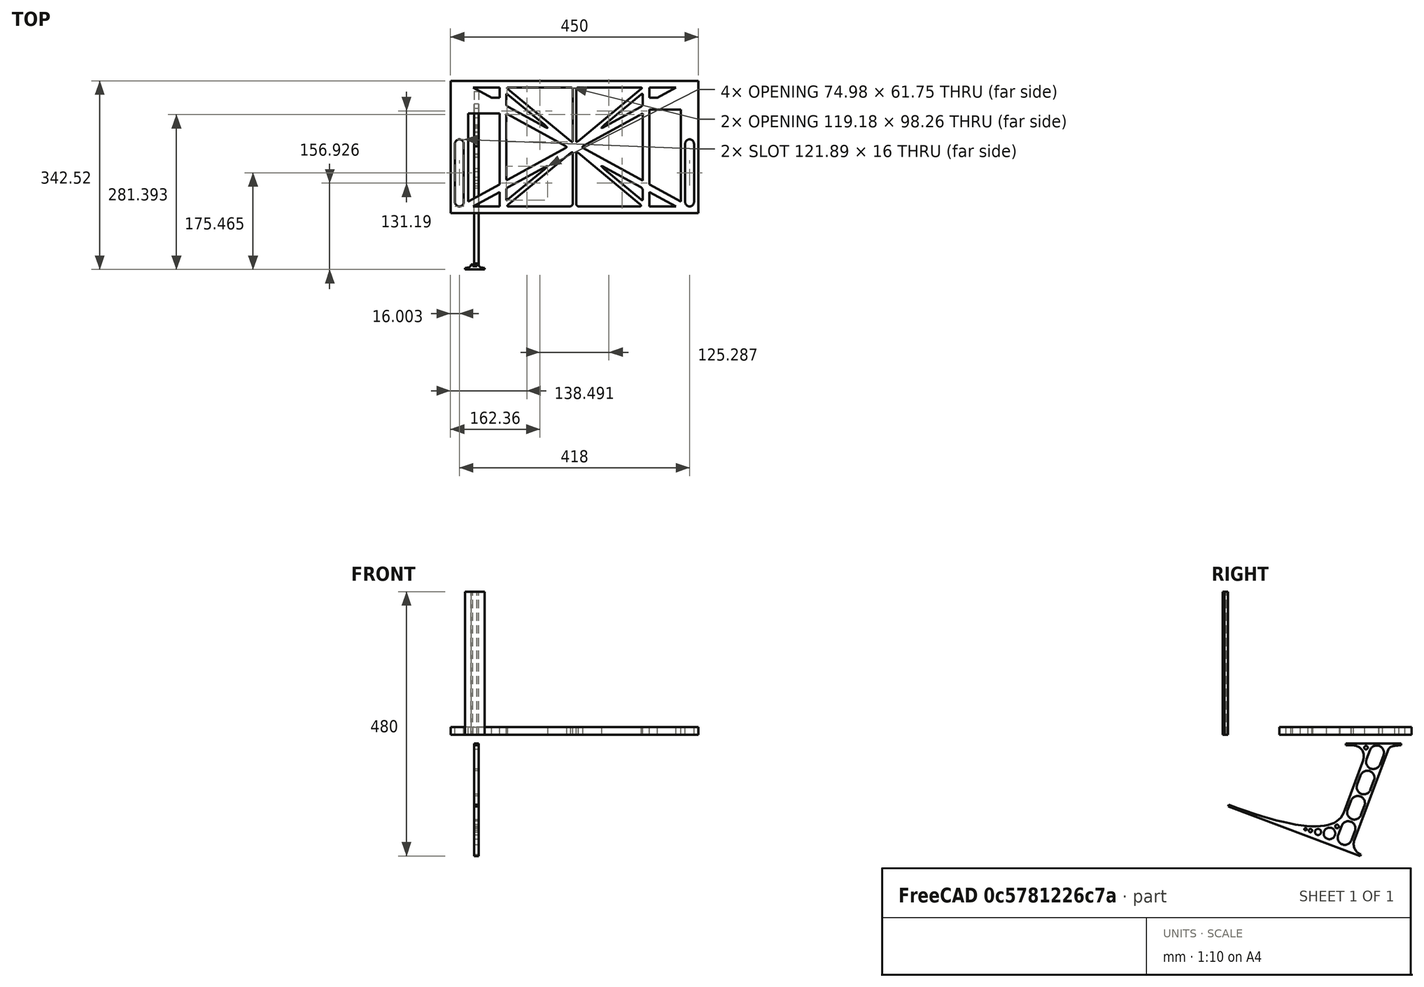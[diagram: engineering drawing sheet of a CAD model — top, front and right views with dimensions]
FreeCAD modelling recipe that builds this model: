
FCSTD DOCUMENT  (FreeCAD 0.19R0.19.2)
Label: laptopStand089
License: All rights reserved
LicenseURL: http://en.wikipedia.org/wiki/All_rights_reserved
objects: Sketcher::SketchObject×3, Part::Extrusion×3
note: 6 computed .brp shape members not serialized (recipe doc carries the construction recipe); baked Part::Feature solids carry a one-line shape summary decoded from their .brp

FEATURE [Sketcher::SketchObject] Sketch
  FullyConstrained = false
  sketch-geometry (236):
    g0: LineSegment StartX=-10.9272 StartY=-82.7794 StartZ=0 EndX=46.0728 EndY=-51.4823 EndZ=0
    g1: LineSegment StartX=366.073 StartY=-91.7794 StartZ=0 EndX=318.073 EndY=-65.424 EndZ=0
    g2: LineSegment StartX=-10.9272 StartY=77.3346 StartZ=0 EndX=-10.9272 EndY=-82.7794 EndZ=0
    g3: LineSegment StartX=375.073 StartY=-82.7794 StartZ=0 EndX=375.073 EndY=83.9235 EndZ=0
    g4: LineSegment StartX=-1.92719 StartY=-91.7794 StartZ=0 EndX=46.0728 EndY=-91.7794 EndZ=0
    g5: LineSegment StartX=318.073 StartY=124.221 StartZ=0 EndX=366.073 EndY=124.221 EndZ=0
    g6: LineSegment StartX=306.073 StartY=77.3346 StartZ=0 EndX=306.073 EndY=-44.8935 EndZ=0
    g7: LineSegment StartX=318.073 StartY=83.9235 StartZ=0 EndX=318.073 EndY=-51.4823 EndZ=0
    g8: LineSegment StartX=318.073 StartY=-51.4823 StartZ=0 EndX=375.073 EndY=-82.7794 EndZ=0
    g9: LineSegment StartX=318.073 StartY=-65.424 StartZ=0 EndX=318.073 EndY=-91.7794 EndZ=0
    g10: LineSegment StartX=318.073 StartY=-91.7794 StartZ=0 EndX=366.073 EndY=-91.7794 EndZ=0
    g11: LineSegment StartX=46.0728 StartY=-65.424 StartZ=0 EndX=-1.92719 EndY=-91.7794 EndZ=0
    g12: LineSegment StartX=46.0728 StartY=-65.424 StartZ=0 EndX=46.0728 EndY=-91.7794 EndZ=0
    g13: LineSegment StartX=46.0728 StartY=77.3346 StartZ=0 EndX=46.0728 EndY=-51.4823 EndZ=0
    g14: LineSegment StartX=-42.9272 StartY=136.221 StartZ=0 EndX=-42.9272 EndY=-103.779 EndZ=0
    g15: LineSegment StartX=407.073 StartY=136.221 StartZ=0 EndX=407.073 EndY=-103.779 EndZ=0
    g16: ArcOfCircle CenterX=-26.9272 CenterY=22.1087 CenterZ=0 NormalX=0 NormalY=0 NormalZ=1 AngleXU=0 Radius=8 StartAngle=1e-16 EndAngle=3.14159
    g17: ArcOfCircle CenterX=-26.9272 CenterY=-83.7794 CenterZ=0 NormalX=0 NormalY=0 NormalZ=1 AngleXU=0 Radius=8 StartAngle=3.14159 EndAngle=6.28319
    g18: LineSegment StartX=-34.9272 StartY=22.1087 StartZ=0 EndX=-34.9272 EndY=-83.7794 EndZ=0
    g19: LineSegment StartX=-18.9272 StartY=22.1087 StartZ=0 EndX=-18.9272 EndY=-83.7794 EndZ=0
    g20: ArcOfCircle CenterX=391.073 CenterY=22.1087 CenterZ=0 NormalX=0 NormalY=0 NormalZ=1 AngleXU=0 Radius=8 StartAngle=-4.4e-15 EndAngle=3.14159
    g21: LineSegment StartX=399.073 StartY=22.1087 StartZ=0 EndX=399.073 EndY=-83.7794 EndZ=0
    g22: LineSegment StartX=383.073 StartY=22.1087 StartZ=0 EndX=383.073 EndY=-83.7794 EndZ=0
    g23: ArcOfCircle CenterX=391.073 CenterY=-83.7794 CenterZ=0 NormalX=0 NormalY=0 NormalZ=1 AngleXU=0 Radius=8 StartAngle=3.14159 EndAngle=6.28319
    g24: Circle CenterX=175.022 CenterY=27.0628 CenterZ=0 NormalX=0 NormalY=0 NormalZ=1 AngleXU=0 Radius=1
    g25: Circle CenterX=179.022 CenterY=24.8665 CenterZ=0 NormalX=0 NormalY=0 NormalZ=1 AngleXU=0 Radius=1
    g26: Circle CenterX=179.022 CenterY=27.0628 CenterZ=0 NormalX=0 NormalY=0 NormalZ=1 AngleXU=0 Radius=1
    g27: BSplineCurve PolesCount=3 KnotsCount=2 Degree=2 IsPeriodic=0
    g28: GeomPoint X=175.022 Y=27.0628 Z=0
    g29: GeomPoint X=179.022 Y=27.0628 Z=0
    g30: Circle CenterX=189.124 CenterY=27.0628 CenterZ=0 NormalX=0 NormalY=0 NormalZ=1 AngleXU=0 Radius=1
    g31: Circle CenterX=185.124 CenterY=24.8665 CenterZ=0 NormalX=0 NormalY=0 NormalZ=1 AngleXU=0 Radius=1
    g32: Circle CenterX=185.124 CenterY=27.0628 CenterZ=0 NormalX=0 NormalY=0 NormalZ=1 AngleXU=0 Radius=1
    g33: BSplineCurve PolesCount=3 KnotsCount=2 Degree=2 IsPeriodic=0
    g34: GeomPoint X=189.124 Y=27.0628 Z=0
    g35: GeomPoint X=185.124 Y=27.0628 Z=0
    g36: Circle CenterX=175.022 CenterY=5.37834 CenterZ=0 NormalX=0 NormalY=0 NormalZ=1 AngleXU=0 Radius=1
    g37: Circle CenterX=179.022 CenterY=7.57463 CenterZ=0 NormalX=0 NormalY=0 NormalZ=1 AngleXU=0 Radius=1
    g38: Circle CenterX=179.022 CenterY=5.34704 CenterZ=0 NormalX=0 NormalY=0 NormalZ=1 AngleXU=0 Radius=1
    g39: BSplineCurve PolesCount=3 KnotsCount=2 Degree=2 IsPeriodic=0
    g40: GeomPoint X=175.022 Y=5.37834 Z=0
    g41: GeomPoint X=179.022 Y=5.34704 Z=0
    g42: Circle CenterX=189.124 CenterY=5.37834 CenterZ=0 NormalX=0 NormalY=0 NormalZ=1 AngleXU=0 Radius=1
    g43: Circle CenterX=185.124 CenterY=7.57463 CenterZ=0 NormalX=0 NormalY=0 NormalZ=1 AngleXU=0 Radius=1
    g44: Circle CenterX=185.124 CenterY=5.34704 CenterZ=0 NormalX=0 NormalY=0 NormalZ=1 AngleXU=0 Radius=1
    g45: BSplineCurve PolesCount=3 KnotsCount=2 Degree=2 IsPeriodic=0
    g46: GeomPoint X=189.124 Y=5.37834 Z=0
    g47: GeomPoint X=185.124 Y=5.34704 Z=0
    g48: Circle CenterX=165.871 CenterY=18.1458 CenterZ=0 NormalX=0 NormalY=0 NormalZ=1 AngleXU=0 Radius=1
    g49: Circle CenterX=169.377 CenterY=16.2206 CenterZ=0 NormalX=0 NormalY=0 NormalZ=1 AngleXU=0 Radius=1
    g50: Circle CenterX=165.871 CenterY=14.2954 CenterZ=0 NormalX=0 NormalY=0 NormalZ=1 AngleXU=0 Radius=1
    g51: BSplineCurve PolesCount=3 KnotsCount=2 Degree=2 IsPeriodic=0
    g52: GeomPoint X=165.871 Y=18.1458 Z=0
    g53: GeomPoint X=165.871 Y=14.2954 Z=0
    g54: Circle CenterX=198.275 CenterY=18.1458 CenterZ=0 NormalX=0 NormalY=0 NormalZ=1 AngleXU=0 Radius=1
    g55: Circle CenterX=194.768 CenterY=16.2206 CenterZ=0 NormalX=0 NormalY=0 NormalZ=1 AngleXU=0 Radius=1
    g56: Circle CenterX=198.275 CenterY=14.2954 CenterZ=0 NormalX=0 NormalY=0 NormalZ=1 AngleXU=0 Radius=1
    g57: BSplineCurve PolesCount=3 KnotsCount=2 Degree=2 IsPeriodic=0
    g58: GeomPoint X=198.275 Y=18.1458 Z=0
    g59: GeomPoint X=198.275 Y=14.2954 Z=0
    g60: LineSegment StartX=198.275 StartY=18.1458 StartZ=0 EndX=306.073 EndY=77.3346 EndZ=0
    g61: LineSegment StartX=198.275 StartY=14.2954 StartZ=0 EndX=306.073 EndY=-44.8935 EndZ=0
    g62: LineSegment StartX=407.073 StartY=-103.779 StartZ=0 EndX=-42.9272 EndY=-103.779 EndZ=0
    g63: LineSegment StartX=407.073 StartY=136.221 StartZ=0 EndX=-42.9272 EndY=136.221 EndZ=0
    g64: LineSegment StartX=46.0728 StartY=77.3346 StartZ=0 EndX=-10.9272 EndY=77.3346 EndZ=0
    g65: LineSegment StartX=46.0728 StartY=105.865 StartZ=0 EndX=31.5028 EndY=105.865 EndZ=0
    g66: LineSegment StartX=46.0728 StartY=124.221 StartZ=0 EndX=46.0728 EndY=105.865 EndZ=0
    g67: LineSegment StartX=-1.92719 StartY=124.221 StartZ=0 EndX=31.5028 EndY=105.865 EndZ=0
    g68: LineSegment StartX=46.0728 StartY=124.221 StartZ=0 EndX=-1.92719 EndY=124.221 EndZ=0
    g69: LineSegment StartX=318.073 StartY=83.9235 StartZ=0 EndX=375.073 EndY=83.9235 EndZ=0
    g70: LineSegment StartX=318.073 StartY=105.865 StartZ=0 EndX=332.643 EndY=105.865 EndZ=0
    g71: LineSegment StartX=332.643 StartY=105.865 StartZ=0 EndX=366.073 EndY=124.221 EndZ=0
    g72: LineSegment StartX=318.073 StartY=124.221 StartZ=0 EndX=318.073 EndY=105.865 EndZ=0
    g73: Circle CenterX=125.607 CenterY=54.1951 CenterZ=0 NormalX=0 NormalY=0 NormalZ=1 AngleXU=0 Radius=1
    g74: Circle CenterX=139.632 CenterY=46.4944 CenterZ=0 NormalX=0 NormalY=0 NormalZ=1 AngleXU=0 Radius=1
    g75: Circle CenterX=127.326 CenterY=56.7187 CenterZ=0 NormalX=0 NormalY=0 NormalZ=1 AngleXU=0 Radius=1
    g76: BSplineCurve PolesCount=3 KnotsCount=2 Degree=2 IsPeriodic=0
    g77: GeomPoint X=125.607 Y=54.1951 Z=0
    g78: GeomPoint X=127.326 Y=56.7187 Z=0
    g79: Circle CenterX=236.821 CenterY=56.7187 CenterZ=0 NormalX=0 NormalY=0 NormalZ=1 AngleXU=0 Radius=1
    g80: Circle CenterX=224.513 CenterY=46.4944 CenterZ=0 NormalX=0 NormalY=0 NormalZ=1 AngleXU=0 Radius=1
    g81: Circle CenterX=238.538 CenterY=54.1951 CenterZ=0 NormalX=0 NormalY=0 NormalZ=1 AngleXU=0 Radius=1
    g82: BSplineCurve PolesCount=3 KnotsCount=2 Degree=2 IsPeriodic=0
    g83: GeomPoint X=236.821 Y=56.7187 Z=0
    g84: GeomPoint X=238.538 Y=54.1951 Z=0
    g85: Circle CenterX=238.538 CenterY=-21.7539 CenterZ=0 NormalX=0 NormalY=0 NormalZ=1 AngleXU=0 Radius=1
    g86: Circle CenterX=224.513 CenterY=-14.0532 CenterZ=0 NormalX=0 NormalY=0 NormalZ=1 AngleXU=0 Radius=1
    g87: Circle CenterX=236.821 CenterY=-24.2775 CenterZ=0 NormalX=0 NormalY=0 NormalZ=1 AngleXU=0 Radius=1
    g88: BSplineCurve PolesCount=3 KnotsCount=2 Degree=2 IsPeriodic=0
    g89: GeomPoint X=238.538 Y=-21.7539 Z=0
    g90: GeomPoint X=236.821 Y=-24.2775 Z=0
    g91: Circle CenterX=125.607 CenterY=-21.7539 CenterZ=0 NormalX=0 NormalY=0 NormalZ=1 AngleXU=0 Radius=1
    g92: Circle CenterX=139.632 CenterY=-14.0532 CenterZ=0 NormalX=0 NormalY=0 NormalZ=1 AngleXU=0 Radius=1
    g93: Circle CenterX=127.325 CenterY=-24.2775 CenterZ=0 NormalX=0 NormalY=0 NormalZ=1 AngleXU=0 Radius=1
    g94: BSplineCurve PolesCount=3 KnotsCount=2 Degree=2 IsPeriodic=0
    g95: GeomPoint X=125.607 Y=-21.7539 Z=0
    g96: GeomPoint X=127.325 Y=-24.2775 Z=0
    g97: Circle CenterX=302.996 CenterY=111.695 CenterZ=0 NormalX=0 NormalY=0 NormalZ=1 AngleXU=0 Radius=1
    g98: Circle CenterX=306.073 CenterY=114.251 CenterZ=0 NormalX=0 NormalY=0 NormalZ=1 AngleXU=0 Radius=1
    g99: Circle CenterX=306.073 CenterY=110.251 CenterZ=0 NormalX=0 NormalY=0 NormalZ=1 AngleXU=0 Radius=1
    g100: BSplineCurve PolesCount=3 KnotsCount=2 Degree=2 IsPeriodic=0
    g101: GeomPoint X=302.996 Y=111.695 Z=0
    g102: GeomPoint X=306.073 Y=110.251 Z=0
    g103: Circle CenterX=306.073 CenterY=95.2763 CenterZ=0 NormalX=0 NormalY=0 NormalZ=1 AngleXU=0 Radius=1
    g104: Circle CenterX=306.073 CenterY=91.2763 CenterZ=0 NormalX=0 NormalY=0 NormalZ=1 AngleXU=0 Radius=1
    g105: Circle CenterX=302.567 CenterY=89.3511 CenterZ=0 NormalX=0 NormalY=0 NormalZ=1 AngleXU=0 Radius=1
    g106: BSplineCurve PolesCount=3 KnotsCount=2 Degree=2 IsPeriodic=0
    g107: GeomPoint X=306.073 Y=95.2763 Z=0
    g108: GeomPoint X=302.567 Y=89.3511 Z=0
    g109: LineSegment StartX=306.073 StartY=110.251 StartZ=0 EndX=306.073 EndY=95.2763 EndZ=0
    g110: LineSegment StartX=302.996 StartY=111.695 StartZ=0 EndX=236.821 EndY=56.7187 EndZ=0
    g111: LineSegment StartX=238.538 StartY=54.1951 StartZ=0 EndX=302.567 EndY=89.3511 EndZ=0
    g112: Circle CenterX=61.1496 CenterY=111.695 CenterZ=0 NormalX=0 NormalY=0 NormalZ=1 AngleXU=0 Radius=1
    g113: Circle CenterX=58.0728 CenterY=114.251 CenterZ=0 NormalX=0 NormalY=0 NormalZ=1 AngleXU=0 Radius=1
    g114: Circle CenterX=58.0728 CenterY=110.251 CenterZ=0 NormalX=0 NormalY=0 NormalZ=1 AngleXU=0 Radius=1
    g115: BSplineCurve PolesCount=3 KnotsCount=2 Degree=2 IsPeriodic=0
    g116: GeomPoint X=61.1496 Y=111.695 Z=0
    g117: GeomPoint X=58.0728 Y=110.251 Z=0
    g118: Circle CenterX=61.5791 CenterY=89.3511 CenterZ=0 NormalX=0 NormalY=0 NormalZ=1 AngleXU=0 Radius=1
    g119: Circle CenterX=58.0728 CenterY=91.2763 CenterZ=0 NormalX=0 NormalY=0 NormalZ=1 AngleXU=0 Radius=1
    g120: Circle CenterX=58.0728 CenterY=95.2763 CenterZ=0 NormalX=0 NormalY=0 NormalZ=1 AngleXU=0 Radius=1
    g121: BSplineCurve PolesCount=3 KnotsCount=2 Degree=2 IsPeriodic=0
    g122: GeomPoint X=61.5791 Y=89.3511 Z=0
    g123: GeomPoint X=58.0728 Y=95.2763 Z=0
    g124: LineSegment StartX=58.0728 StartY=110.251 StartZ=0 EndX=58.0728 EndY=95.2763 EndZ=0
    g125: LineSegment StartX=61.1496 StartY=111.695 StartZ=0 EndX=127.326 EndY=56.7187 EndZ=0
    g126: LineSegment StartX=125.607 StartY=54.1951 StartZ=0 EndX=61.5791 EndY=89.3511 EndZ=0
    g127: Circle CenterX=61.5791 CenterY=-56.9099 CenterZ=0 NormalX=0 NormalY=0 NormalZ=1 AngleXU=0 Radius=1
    g128: Circle CenterX=58.0728 CenterY=-58.8351 CenterZ=0 NormalX=0 NormalY=0 NormalZ=1 AngleXU=0 Radius=1
    g129: Circle CenterX=58.0728 CenterY=-62.8351 CenterZ=0 NormalX=0 NormalY=0 NormalZ=1 AngleXU=0 Radius=1
    g130: BSplineCurve PolesCount=3 KnotsCount=2 Degree=2 IsPeriodic=0
    g131: GeomPoint X=61.5791 Y=-56.9099 Z=0
    g132: GeomPoint X=58.0728 Y=-62.8351 Z=0
    g133: Circle CenterX=58.0728 CenterY=-77.8102 CenterZ=0 NormalX=0 NormalY=0 NormalZ=1 AngleXU=0 Radius=1
    g134: Circle CenterX=58.0728 CenterY=-81.8102 CenterZ=0 NormalX=0 NormalY=0 NormalZ=1 AngleXU=0 Radius=1
    g135: Circle CenterX=61.1496 CenterY=-79.2541 CenterZ=0 NormalX=0 NormalY=0 NormalZ=1 AngleXU=0 Radius=1
    g136: BSplineCurve PolesCount=3 KnotsCount=2 Degree=2 IsPeriodic=0
    g137: GeomPoint X=58.0728 Y=-77.8102 Z=0
    g138: GeomPoint X=61.1496 Y=-79.2541 Z=0
    g139: LineSegment StartX=58.0728 StartY=-62.8351 StartZ=0 EndX=58.0728 EndY=-77.8102 EndZ=0
    g140: LineSegment StartX=61.1496 StartY=-79.2541 StartZ=0 EndX=127.325 EndY=-24.2775 EndZ=0
    g141: LineSegment StartX=125.607 StartY=-21.7539 StartZ=0 EndX=61.5791 EndY=-56.9099 EndZ=0
    g142: Circle CenterX=302.567 CenterY=-56.9099 CenterZ=0 NormalX=0 NormalY=0 NormalZ=1 AngleXU=0 Radius=1
    g143: Circle CenterX=306.073 CenterY=-58.8351 CenterZ=0 NormalX=0 NormalY=0 NormalZ=1 AngleXU=0 Radius=1
    g144: Circle CenterX=306.073 CenterY=-62.8351 CenterZ=0 NormalX=0 NormalY=0 NormalZ=1 AngleXU=0 Radius=1
    g145: BSplineCurve PolesCount=3 KnotsCount=2 Degree=2 IsPeriodic=0
    g146: GeomPoint X=302.567 Y=-56.9099 Z=0
    g147: GeomPoint X=306.073 Y=-62.8351 Z=0
    g148: Circle CenterX=302.996 CenterY=-79.2541 CenterZ=0 NormalX=0 NormalY=0 NormalZ=1 AngleXU=0 Radius=1
    g149: Circle CenterX=306.073 CenterY=-81.8102 CenterZ=0 NormalX=0 NormalY=0 NormalZ=1 AngleXU=0 Radius=1
    g150: Circle CenterX=306.073 CenterY=-77.8102 CenterZ=0 NormalX=0 NormalY=0 NormalZ=1 AngleXU=0 Radius=1
    g151: BSplineCurve PolesCount=3 KnotsCount=2 Degree=2 IsPeriodic=0
    g152: GeomPoint X=302.996 Y=-79.2541 Z=0
    g153: GeomPoint X=306.073 Y=-77.8102 Z=0
    g154: LineSegment StartX=306.073 StartY=-62.8351 StartZ=0 EndX=306.073 EndY=-77.8102 EndZ=0
    g155: LineSegment StartX=302.996 StartY=-79.2541 StartZ=0 EndX=236.821 EndY=-24.2775 EndZ=0
    g156: LineSegment StartX=238.538 StartY=-21.7539 StartZ=0 EndX=302.567 EndY=-56.9099 EndZ=0
    g157: Circle CenterX=61.6457 CenterY=-88.8112 CenterZ=0 NormalX=0 NormalY=0 NormalZ=1 AngleXU=0 Radius=1
    g158: Circle CenterX=58.0728 CenterY=-91.7794 CenterZ=0 NormalX=0 NormalY=0 NormalZ=1 AngleXU=0 Radius=1
    g159: Circle CenterX=63.9135 CenterY=-91.7794 CenterZ=0 NormalX=0 NormalY=0 NormalZ=1 AngleXU=0 Radius=1
    g160: BSplineCurve PolesCount=3 KnotsCount=2 Degree=2 IsPeriodic=0
    g161: GeomPoint X=61.6457 Y=-88.8112 Z=0
    g162: GeomPoint X=63.9135 Y=-91.7794 Z=0
    g163: Circle CenterX=179.022 CenterY=-85.8163 CenterZ=0 NormalX=0 NormalY=0 NormalZ=1 AngleXU=0 Radius=1
    g164: Circle CenterX=179.022 CenterY=-91.7794 CenterZ=0 NormalX=0 NormalY=0 NormalZ=1 AngleXU=0 Radius=1
    g165: Circle CenterX=171.895 CenterY=-91.7794 CenterZ=0 NormalX=0 NormalY=0 NormalZ=1 AngleXU=0 Radius=1
    g166: BSplineCurve PolesCount=3 KnotsCount=2 Degree=2 IsPeriodic=0
    g167: GeomPoint X=179.022 Y=-85.8163 Z=0
    g168: GeomPoint X=171.895 Y=-91.7794 Z=0
    g169: Circle CenterX=185.124 CenterY=-86.2028 CenterZ=0 NormalX=0 NormalY=0 NormalZ=1 AngleXU=0 Radius=1
    g170: Circle CenterX=185.124 CenterY=-91.7794 CenterZ=0 NormalX=0 NormalY=0 NormalZ=1 AngleXU=0 Radius=1
    g171: Circle CenterX=191.747 CenterY=-91.7794 CenterZ=0 NormalX=0 NormalY=0 NormalZ=1 AngleXU=0 Radius=1
    g172: BSplineCurve PolesCount=3 KnotsCount=2 Degree=2 IsPeriodic=0
    g173: GeomPoint X=185.124 Y=-86.2028 Z=0
    g174: GeomPoint X=191.747 Y=-91.7794 Z=0
    g175: Circle CenterX=299.888 CenterY=-86.6413 CenterZ=0 NormalX=0 NormalY=0 NormalZ=1 AngleXU=0 Radius=1
    g176: Circle CenterX=306.073 CenterY=-91.7794 CenterZ=0 NormalX=0 NormalY=0 NormalZ=1 AngleXU=0 Radius=1
    g177: Circle CenterX=298.776 CenterY=-91.7794 CenterZ=0 NormalX=0 NormalY=0 NormalZ=1 AngleXU=0 Radius=1
    g178: BSplineCurve PolesCount=3 KnotsCount=2 Degree=2 IsPeriodic=0
    g179: GeomPoint X=299.888 Y=-86.6413 Z=0
    g180: GeomPoint X=298.776 Y=-91.7794 Z=0
    g181: LineSegment StartX=189.124 StartY=5.37834 StartZ=0 EndX=299.888 EndY=-86.6413 EndZ=0
    g182: LineSegment StartX=298.776 StartY=-91.7794 StartZ=0 EndX=191.747 EndY=-91.7794 EndZ=0
    g183: LineSegment StartX=185.124 StartY=-86.2028 StartZ=0 EndX=185.124 EndY=5.34704 EndZ=0
    g184: LineSegment StartX=179.022 StartY=5.34704 StartZ=0 EndX=179.022 EndY=-85.8163 EndZ=0
    g185: LineSegment StartX=171.895 StartY=-91.7794 StartZ=0 EndX=63.9135 EndY=-91.7794 EndZ=0
    g186: LineSegment StartX=61.6457 StartY=-88.8112 StartZ=0 EndX=175.022 EndY=5.37834 EndZ=0
    g187: Circle CenterX=302.073 CenterY=124.221 CenterZ=0 NormalX=0 NormalY=0 NormalZ=1 AngleXU=0 Radius=1
    g188: Circle CenterX=306.073 CenterY=124.221 CenterZ=0 NormalX=0 NormalY=0 NormalZ=1 AngleXU=0 Radius=1
    g189: Circle CenterX=302.996 CenterY=121.665 CenterZ=0 NormalX=0 NormalY=0 NormalZ=1 AngleXU=0 Radius=1
    g190: BSplineCurve PolesCount=3 KnotsCount=2 Degree=2 IsPeriodic=0
    g191: GeomPoint X=302.073 Y=124.221 Z=0
    g192: GeomPoint X=302.996 Y=121.665 Z=0
    g193: Circle CenterX=189.124 CenterY=124.221 CenterZ=0 NormalX=0 NormalY=0 NormalZ=1 AngleXU=0 Radius=1
    g194: Circle CenterX=185.124 CenterY=124.221 CenterZ=0 NormalX=0 NormalY=0 NormalZ=1 AngleXU=0 Radius=1
    g195: Circle CenterX=185.124 CenterY=120.221 CenterZ=0 NormalX=0 NormalY=0 NormalZ=1 AngleXU=0 Radius=1
    g196: BSplineCurve PolesCount=3 KnotsCount=2 Degree=2 IsPeriodic=0
    g197: GeomPoint X=189.124 Y=124.221 Z=0
    g198: GeomPoint X=185.124 Y=120.221 Z=0
    g199: Circle CenterX=175.022 CenterY=124.221 CenterZ=0 NormalX=0 NormalY=0 NormalZ=1 AngleXU=0 Radius=1
    g200: Circle CenterX=179.022 CenterY=124.221 CenterZ=0 NormalX=0 NormalY=0 NormalZ=1 AngleXU=0 Radius=1
    g201: Circle CenterX=179.022 CenterY=120.221 CenterZ=0 NormalX=0 NormalY=0 NormalZ=1 AngleXU=0 Radius=1
    g202: BSplineCurve PolesCount=3 KnotsCount=2 Degree=2 IsPeriodic=0
    g203: GeomPoint X=175.022 Y=124.221 Z=0
    g204: GeomPoint X=179.022 Y=120.221 Z=0
    g205: Circle CenterX=62.0728 CenterY=124.221 CenterZ=0 NormalX=0 NormalY=0 NormalZ=1 AngleXU=0 Radius=1
    g206: Circle CenterX=58.0728 CenterY=124.221 CenterZ=0 NormalX=0 NormalY=0 NormalZ=1 AngleXU=0 Radius=1
    g207: Circle CenterX=61.1496 CenterY=121.665 CenterZ=0 NormalX=0 NormalY=0 NormalZ=1 AngleXU=0 Radius=1
    g208: BSplineCurve PolesCount=3 KnotsCount=2 Degree=2 IsPeriodic=0
    g209: GeomPoint X=62.0728 Y=124.221 Z=0
    g210: GeomPoint X=61.1496 Y=121.665 Z=0
    g211: LineSegment StartX=62.0728 StartY=124.221 StartZ=0 EndX=175.022 EndY=124.221 EndZ=0
    g212: LineSegment StartX=179.022 StartY=120.221 StartZ=0 EndX=179.022 EndY=27.0628 EndZ=0
    g213: LineSegment StartX=185.124 StartY=27.0628 StartZ=0 EndX=185.124 EndY=120.221 EndZ=0
    g214: LineSegment StartX=189.124 StartY=124.221 StartZ=0 EndX=302.073 EndY=124.221 EndZ=0
    g215: LineSegment StartX=302.996 StartY=121.665 StartZ=0 EndX=189.124 EndY=27.0628 EndZ=0
    g216: LineSegment StartX=175.022 StartY=27.0628 StartZ=0 EndX=61.1496 EndY=121.665 EndZ=0
    g217: Circle CenterX=61.5791 CenterY=75.4095 CenterZ=0 NormalX=0 NormalY=0 NormalZ=1 AngleXU=0 Radius=1
    g218: Circle CenterX=58.0728 CenterY=77.3346 CenterZ=0 NormalX=0 NormalY=0 NormalZ=1 AngleXU=0 Radius=1
    g219: Circle CenterX=58.0728 CenterY=73.3346 CenterZ=0 NormalX=0 NormalY=0 NormalZ=1 AngleXU=0 Radius=1
    g220: BSplineCurve PolesCount=3 KnotsCount=2 Degree=2 IsPeriodic=0
    g221: GeomPoint X=61.5791 Y=75.4095 Z=0
    g222: GeomPoint X=58.0728 Y=73.3346 Z=0
    g223: Circle CenterX=58.0728 CenterY=-40.8935 CenterZ=0 NormalX=0 NormalY=0 NormalZ=1 AngleXU=0 Radius=1
    g224: Circle CenterX=58.0728 CenterY=-44.8935 CenterZ=0 NormalX=0 NormalY=0 NormalZ=1 AngleXU=0 Radius=1
    g225: Circle CenterX=61.5791 CenterY=-42.9683 CenterZ=0 NormalX=0 NormalY=0 NormalZ=1 AngleXU=0 Radius=1
    g226: BSplineCurve PolesCount=3 KnotsCount=2 Degree=2 IsPeriodic=0
    g227: GeomPoint X=58.0728 Y=-40.8935 Z=0
    g228: GeomPoint X=61.5791 Y=-42.9683 Z=0
    g229: LineSegment StartX=61.5791 StartY=-42.9683 StartZ=0 EndX=165.871 EndY=14.2954 EndZ=0
    g230: LineSegment StartX=165.871 StartY=18.1458 StartZ=0 EndX=61.5791 EndY=75.4095 EndZ=0
    g231: LineSegment StartX=58.0728 StartY=73.3346 StartZ=0 EndX=58.0728 EndY=-40.8935 EndZ=0
    g232: LineSegment StartX=306.994 StartY=77.7433 StartZ=0 EndX=306.994 EndY=73.7433 EndZ=0
    g233: LineSegment StartX=305.944 StartY=78.0104 StartZ=0 EndX=302.438 EndY=76.0852 EndZ=0
    g234: LineSegment StartX=307.626 StartY=-43.3024 StartZ=0 EndX=307.626 EndY=-39.3024 EndZ=0
    g235: LineSegment StartX=303.392 StartY=-44.772 StartZ=0 EndX=299.886 EndY=-42.8468 EndZ=0
  constraints (403):
    c: Horizontal(g4)
    c: Horizontal(g5)
    c: Coincident(g7,g8)
    c: Coincident(g9,g1)
    c: Tangent(g7,g9)
    c: Coincident(g12,g11)
    c: Coincident(g0,g13)
    c: Block(g8)
    c: Block(g3)
    c: Block(g1)
    c: Block(g9)
    c: Block(g12)
    c: Block(g11)
    c: Block(g0)
    c: Block(g2)
    c: Block(g6)
    c: Block(g5)
    c: Block(g10)
    c: Block(g4)
    c: Vertical(g14)
    c: Vertical(g15)
    c: Block(g15)
    c: Block(g14)
    c: Tangent(g16,g19) = 1.5708
    c: Tangent(g16,g18) = -1.5708
    c: Tangent(g18,g17) = -1.5708
    c: Tangent(g19,g17) = 1.5708
    c: Vertical(g18)
    c: Equal(g16,g17)
    c: Block(g19)
    c: Block(g18)
    c: Tangent(g20,g21) = 1.5708
    c: Tangent(g21,g23) = 1.5708
    c: Equal(g20,g23)
    c: Coincident(g22,g20)
    c: Coincident(g22,g23)
    c: Block(g21)
    c: Block(g22)
    c: Weight(g24) = 1
    c: Equal(g24,g25)
    c: Equal(g24,g26)
    c: InternalAlignment(g24,g27)
    c: InternalAlignment(g25,g27)
    c: InternalAlignment(g26,g27)
    c: InternalAlignment(g28,g27)
    c: InternalAlignment(g29,g27)
    c: Weight(g30) = 1
    c: Equal(g30,g31)
    c: Equal(g30,g32)
    c: InternalAlignment(g30,g33)
    c: InternalAlignment(g31,g33)
    c: InternalAlignment(g32,g33)
    c: InternalAlignment(g34,g33)
    c: InternalAlignment(g35,g33)
    c: Block(g33)
    c: Block(g27)
    c: Weight(g36) = 1
    c: Equal(g36,g37)
    c: Equal(g36,g38)
    c: InternalAlignment(g36,g39)
    c: InternalAlignment(g37,g39)
    c: InternalAlignment(g38,g39)
    c: InternalAlignment(g40,g39)
    c: InternalAlignment(g41,g39)
    c: Weight(g42) = 1
    c: Equal(g42,g43)
    c: Equal(g42,g44)
    c: InternalAlignment(g42,g45)
    c: InternalAlignment(g43,g45)
    c: InternalAlignment(g44,g45)
    c: InternalAlignment(g46,g45)
    c: InternalAlignment(g47,g45)
    c: Block(g45)
    c: Block(g39)
    c: Weight(g48) = 1
    c: Equal(g48,g49)
    c: Equal(g48,g50)
    c: InternalAlignment(g48,g51)
    c: InternalAlignment(g49,g51)
    c: InternalAlignment(g50,g51)
    c: InternalAlignment(g52,g51)
    c: InternalAlignment(g53,g51)
    c: Weight(g54) = 1
    c: Equal(g54,g55)
    c: Equal(g54,g56)
    c: InternalAlignment(g54,g57)
    c: InternalAlignment(g55,g57)
    c: InternalAlignment(g56,g57)
    c: InternalAlignment(g58,g57)
    c: InternalAlignment(g59,g57)
    c: Block(g51)
    c: Block(g57)
    c: Coincident(g60,g57)
    c: Coincident(g60,g6)
    c: Coincident(g61,g57)
    c: Coincident(g61,g6)
    c: Coincident(g62,g15)
    c: Coincident(g62,g14)
    c: Horizontal(g62)
    c: Distance(g62) = 450
    c: Coincident(g63,g15)
    c: Coincident(g63,g14)
    c: Horizontal(g63)
    c: Horizontal(g64)
    c: Coincident(g13,g64)
    c: Horizontal(g65)
    c: Vertical(g66)
    c: Block(g66)
    c: Block(g65)
    c: Block(g64)
    c: Distance(g66) = 18.3554
    c: Coincident(g68,g66)
    c: Coincident(g68,g67)
    c: Horizontal(g68)
    c: Block(g68)
    c: Block(g67)
    c: Coincident(g65,g67)
    c: Coincident(g2,g64)
    c: Coincident(g69,g7)
    c: Horizontal(g69)
    c: Horizontal(g70)
    c: Block(g69)
    c: Coincident(g71,g5)
    c: Coincident(g72,g5)
    c: Coincident(g72,g70)
    c: Vertical(g72)
    c: Block(g72)
    c: Coincident(g70,g71)
    c: Block(g71)
    c: Coincident(g3,g69)
    c: Weight(g73) = 1
    c: Equal(g73,g74)
    c: Equal(g73,g75)
    c: InternalAlignment(g73,g76)
    c: InternalAlignment(g74,g76)
    c: InternalAlignment(g75,g76)
    c: InternalAlignment(g77,g76)
    c: InternalAlignment(g78,g76)
    c: Block(g76)
    c: Weight(g79) = 1
    c: Equal(g79,g80)
    c: Equal(g79,g81)
    c: InternalAlignment(g79,g82)
    c: InternalAlignment(g80,g82)
    c: InternalAlignment(g81,g82)
    c: InternalAlignment(g83,g82)
    c: InternalAlignment(g84,g82)
    c: Block(g82)
    c: Weight(g85) = 1
    c: Equal(g85,g86)
    c: Equal(g85,g87)
    c: InternalAlignment(g85,g88)
    c: InternalAlignment(g86,g88)
    c: InternalAlignment(g87,g88)
    c: InternalAlignment(g89,g88)
    c: InternalAlignment(g90,g88)
    c: Block(g88)
    c: Weight(g91) = 1
    c: Equal(g91,g92)
    c: Equal(g91,g93)
    c: InternalAlignment(g91,g94)
    c: InternalAlignment(g92,g94)
    c: InternalAlignment(g93,g94)
    c: InternalAlignment(g95,g94)
    c: InternalAlignment(g96,g94)
    c: Block(g94)
    c: Weight(g97) = 1
    c: Equal(g97,g98)
    c: Equal(g97,g99)
    c: InternalAlignment(g97,g100)
    c: InternalAlignment(g98,g100)
    c: InternalAlignment(g99,g100)
    c: InternalAlignment(g101,g100)
    c: InternalAlignment(g102,g100)
    c: Weight(g103) = 1
    c: Equal(g103,g104)
    c: Equal(g103,g105)
    c: InternalAlignment(g103,g106)
    c: InternalAlignment(g104,g106)
    c: InternalAlignment(g105,g106)
    c: InternalAlignment(g107,g106)
    c: InternalAlignment(g108,g106)
    c: Block(g100)
    c: Block(g106)
    c: Coincident(g109,g100)
    c: Coincident(g109,g106)
    c: Vertical(g109)
    c: Coincident(g110,g100)
    c: Coincident(g110,g82)
    c: Coincident(g111,g82)
    c: Coincident(g111,g106)
    c: Weight(g112) = 1
    c: Equal(g112,g113)
    c: Equal(g112,g114)
    c: InternalAlignment(g112,g115)
    c: InternalAlignment(g113,g115)
    c: InternalAlignment(g114,g115)
    c: InternalAlignment(g116,g115)
    c: InternalAlignment(g117,g115)
    c: Weight(g118) = 1
    c: Equal(g118,g119)
    c: Equal(g118,g120)
    c: InternalAlignment(g118,g121)
    c: InternalAlignment(g119,g121)
    c: InternalAlignment(g120,g121)
    c: InternalAlignment(g122,g121)
    c: InternalAlignment(g123,g121)
    c: Block(g115)
    c: Block(g121)
    c: Coincident(g124,g115)
    c: Coincident(g124,g121)
    c: Vertical(g124)
    c: Coincident(g125,g115)
    c: Coincident(g125,g76)
    c: Coincident(g126,g76)
    c: Coincident(g126,g121)
    c: Weight(g127) = 1
    c: Equal(g127,g128)
    c: Equal(g127,g129)
    c: InternalAlignment(g127,g130)
    c: InternalAlignment(g128,g130)
    c: InternalAlignment(g129,g130)
    c: InternalAlignment(g131,g130)
    c: InternalAlignment(g132,g130)
    c: Weight(g133) = 1
    c: Equal(g133,g134)
    c: Equal(g133,g135)
    c: InternalAlignment(g133,g136)
    c: InternalAlignment(g134,g136)
    c: InternalAlignment(g135,g136)
    c: InternalAlignment(g137,g136)
    c: InternalAlignment(g138,g136)
    c: Block(g130)
    c: Block(g136)
    c: Coincident(g139,g130)
    c: Coincident(g139,g136)
    c: Vertical(g139)
    c: Coincident(g140,g136)
    c: Coincident(g140,g94)
    c: Coincident(g141,g94)
    c: Coincident(g141,g130)
    c: Weight(g142) = 1
    c: Equal(g142,g143)
    c: Equal(g142,g144)
    c: InternalAlignment(g142,g145)
    c: InternalAlignment(g143,g145)
    c: InternalAlignment(g144,g145)
    c: InternalAlignment(g146,g145)
    c: InternalAlignment(g147,g145)
    c: Weight(g148) = 1
    c: Equal(g148,g149)
    c: Equal(g148,g150)
    c: InternalAlignment(g148,g151)
    c: InternalAlignment(g149,g151)
    c: InternalAlignment(g150,g151)
    c: InternalAlignment(g152,g151)
    c: InternalAlignment(g153,g151)
    c: Block(g145)
    c: Block(g151)
    c: Coincident(g154,g145)
    c: Coincident(g154,g151)
    c: Vertical(g154)
    c: Coincident(g155,g151)
    c: Coincident(g155,g88)
    c: Coincident(g156,g88)
    c: Coincident(g156,g145)
    c: Weight(g157) = 1
    c: Equal(g157,g158)
    c: Equal(g157,g159)
    c: InternalAlignment(g157,g160)
    c: InternalAlignment(g158,g160)
    c: InternalAlignment(g159,g160)
    c: InternalAlignment(g161,g160)
    c: InternalAlignment(g162,g160)
    c: Weight(g163) = 1
    c: Equal(g163,g164)
    c: Equal(g163,g165)
    c: InternalAlignment(g163,g166)
    c: InternalAlignment(g164,g166)
    c: InternalAlignment(g165,g166)
    c: InternalAlignment(g167,g166)
    c: InternalAlignment(g168,g166)
    c: Weight(g169) = 1
    c: Equal(g169,g170)
    c: Equal(g169,g171)
    c: InternalAlignment(g169,g172)
    c: InternalAlignment(g170,g172)
    c: InternalAlignment(g171,g172)
    c: InternalAlignment(g173,g172)
    c: InternalAlignment(g174,g172)
    c: Weight(g175) = 1
    c: Equal(g175,g176)
    c: Equal(g175,g177)
    c: InternalAlignment(g175,g178)
    c: InternalAlignment(g176,g178)
    c: InternalAlignment(g177,g178)
    c: InternalAlignment(g179,g178)
    c: InternalAlignment(g180,g178)
    c: Block(g178)
    c: Block(g172)
    c: Block(g166)
    c: Block(g160)
    c: Coincident(g181,g45)
    c: Coincident(g181,g178)
    c: Coincident(g182,g178)
    c: Coincident(g182,g172)
    c: Horizontal(g182)
    c: Coincident(g183,g172)
    c: Coincident(g183,g45)
    c: Vertical(g183)
    c: Coincident(g184,g39)
    c: Coincident(g184,g166)
    c: Vertical(g184)
    c: Coincident(g185,g166)
    c: Coincident(g185,g160)
    c: Horizontal(g185)
    c: Coincident(g186,g160)
    c: Coincident(g186,g39)
    c: Weight(g187) = 1
    c: Equal(g187,g188)
    c: Equal(g187,g189)
    c: InternalAlignment(g187,g190)
    c: InternalAlignment(g188,g190)
    c: InternalAlignment(g189,g190)
    c: InternalAlignment(g191,g190)
    c: InternalAlignment(g192,g190)
    c: Weight(g193) = 1
    c: Equal(g193,g194)
    c: Equal(g193,g195)
    c: InternalAlignment(g193,g196)
    c: InternalAlignment(g194,g196)
    c: InternalAlignment(g195,g196)
    c: InternalAlignment(g197,g196)
    c: InternalAlignment(g198,g196)
    c: Weight(g199) = 1
    c: Equal(g199,g200)
    c: Equal(g199,g201)
    c: InternalAlignment(g199,g202)
    c: InternalAlignment(g200,g202)
    c: InternalAlignment(g201,g202)
    c: InternalAlignment(g203,g202)
    c: InternalAlignment(g204,g202)
    c: Weight(g205) = 1
    c: Equal(g205,g206)
    c: Equal(g205,g207)
    c: InternalAlignment(g205,g208)
    c: InternalAlignment(g206,g208)
    c: InternalAlignment(g207,g208)
    c: InternalAlignment(g209,g208)
    c: InternalAlignment(g210,g208)
    c: Block(g208)
    c: Block(g202)
    c: Block(g196)
    c: Block(g190)
    c: Coincident(g211,g208)
    c: Coincident(g211,g202)
    c: Horizontal(g211)
    c: Coincident(g212,g202)
    c: Coincident(g212,g27)
    c: Vertical(g212)
    c: Coincident(g213,g33)
    c: Coincident(g213,g196)
    c: Vertical(g213)
    c: Coincident(g214,g196)
    c: Coincident(g214,g190)
    c: Horizontal(g214)
    c: Coincident(g215,g190)
    c: Coincident(g215,g33)
    c: Coincident(g216,g27)
    c: Coincident(g216,g208)
    c: Weight(g217) = 1
    c: Equal(g217,g218)
    c: Equal(g217,g219)
    c: InternalAlignment(g217,g220)
    c: InternalAlignment(g218,g220)
    c: InternalAlignment(g219,g220)
    c: InternalAlignment(g221,g220)
    c: InternalAlignment(g222,g220)
    c: Weight(g223) = 1
    c: Equal(g223,g224)
    c: Equal(g223,g225)
    c: InternalAlignment(g223,g226)
    c: InternalAlignment(g224,g226)
    c: InternalAlignment(g225,g226)
    c: InternalAlignment(g227,g226)
    c: InternalAlignment(g228,g226)
    c: Block(g226)
    c: Block(g220)
    c: Coincident(g229,g226)
    c: Coincident(g229,g51)
    c: Coincident(g230,g51)
    c: Coincident(g230,g220)
    c: Coincident(g231,g220)
    c: Coincident(g231,g226)
    c: Vertical(g231)
    c: Vertical(g232)
    c: Vertical(g234)
    c: Parallel(g61,g235)
    c: Parallel(g233,g60)
    c: Distance(g233) = 4
    c: Distance(g232) = 4
    c: Distance(g234) = 4
    c: Distance(g235) = 4
FEATURE [Sketcher::SketchObject] Sketch001
  FullyConstrained = true
  MapMode = 4
  Placement = pos=(0,0,0) rot=(0.57735,0.57735,0.57735;2.0944rad)
  Support = -> [Sketch]
  sketch-geometry (46):
    g0: BSplineCurve PolesCount=3 KnotsCount=2 Degree=2 IsPeriodic=0
    g1: ArcOfCircle CenterX=73.1223 CenterY=-32.291 CenterZ=0 NormalX=0 NormalY=0 NormalZ=1 AngleXU=0 Radius=13 StartAngle=5.92268 EndAngle=9.06428
    g2: ArcOfCircle CenterX=66.7816 CenterY=-49.1439 CenterZ=0 NormalX=0 NormalY=0 NormalZ=1 AngleXU=0 Radius=13 StartAngle=2.78068 EndAngle=5.92131
    g3: ArcOfCircle CenterX=55.9263 CenterY=-78.1807 CenterZ=0 NormalX=0 NormalY=0 NormalZ=1 AngleXU=0 Radius=13 StartAngle=5.92268 EndAngle=9.06428
    g4: ArcOfCircle CenterX=49.5884 CenterY=-95.0342 CenterZ=0 NormalX=0 NormalY=0 NormalZ=1 AngleXU=0 Radius=13 StartAngle=2.78068 EndAngle=5.92131
    g5: ArcOfCircle CenterX=38.7206 CenterY=-124.067 CenterZ=0 NormalX=0 NormalY=0 NormalZ=1 AngleXU=0 Radius=13 StartAngle=5.92268 EndAngle=9.06428
    g6: ArcOfCircle CenterX=32.3875 CenterY=-140.92 CenterZ=0 NormalX=0 NormalY=0 NormalZ=1 AngleXU=0 Radius=13 StartAngle=2.78068 EndAngle=5.92131
    g7: ArcOfCircle CenterX=21.4715 CenterY=-169.934 CenterZ=0 NormalX=0 NormalY=0 NormalZ=1 AngleXU=0 Radius=13 StartAngle=5.92268 EndAngle=9.06428
    g8: ArcOfCircle CenterX=15.1336 CenterY=-186.787 CenterZ=0 NormalX=0 NormalY=0 NormalZ=1 AngleXU=0 Radius=13 StartAngle=2.78068 EndAngle=5.92131
    g9-g12: Circle x4 (B-spline internal-alignment scaffolding for g13; pole/knot coordinates omitted)
    g13: BSplineCurve PolesCount=4 KnotsCount=2 Degree=3 IsPeriodic=0
    g14: GeomPoint X=28.8094 Y=-19.0875 Z=0
    g15: GeomPoint X=47.0443 Y=-50.4712 Z=0
    g16: Circle CenterX=53.5586 CenterY=-23.2695 CenterZ=0 NormalX=0 NormalY=0 NormalZ=1 AngleXU=0 Radius=3.24518
    g17: Circle CenterX=-195.441 CenterY=-127.082 CenterZ=0 NormalX=0 NormalY=0 NormalZ=1 AngleXU=0 Radius=1
    g18: Circle CenterX=-8.24091 CenterY=-197.481 CenterZ=0 NormalX=0 NormalY=0 NormalZ=1 AngleXU=0 Radius=1
    g19: Circle CenterX=12.8789 CenterY=-141.321 CenterZ=0 NormalX=0 NormalY=0 NormalZ=1 AngleXU=0 Radius=1
    g20: BSplineCurve PolesCount=3 KnotsCount=2 Degree=2 IsPeriodic=0
    g21: GeomPoint X=-195.441 Y=-127.082 Z=0
    g22: GeomPoint X=12.8789 Y=-141.321 Z=0
    g23: Circle CenterX=-12.8016 CenterY=-179.036 CenterZ=0 NormalX=0 NormalY=0 NormalZ=1 AngleXU=0 Radius=10.5072
    g24: Circle CenterX=0.933922 CenterY=-166.43 CenterZ=0 NormalX=0 NormalY=0 NormalZ=1 AngleXU=0 Radius=3.26661
    g25: Circle CenterX=-33.5518 CenterY=-176.44 CenterZ=0 NormalX=0 NormalY=0 NormalZ=1 AngleXU=0 Radius=5.64388
    g26: Circle CenterX=-47.2366 CenterY=-173.859 CenterZ=0 NormalX=0 NormalY=0 NormalZ=1 AngleXU=0 Radius=3.01653
    g27: Circle CenterX=-56.2595 CenterY=-171.456 CenterZ=0 NormalX=0 NormalY=0 NormalZ=1 AngleXU=0 Radius=2.12826
    g28: ArcOfCircle CenterX=51.2151 CenterY=-198.473 CenterZ=0 NormalX=0 NormalY=0 NormalZ=1 AngleXU=0 Radius=20 StartAngle=2.78189 EndAngle=4.35269
    g29: LineSegment StartX=32.4951 StartY=-191.433 StartZ=0 EndX=94.6578 EndY=-26.1352 EndZ=0
    g30: LineSegment StartX=43.1192 StartY=-220.001 StartZ=0 EndX=-196.497 EndY=-129.89 EndZ=0
    g31: LineSegment StartX=43.1192 StartY=-220.001 StartZ=0 EndX=44.1752 EndY=-217.193 EndZ=0
    g32: LineSegment StartX=117.223 StartY=-19.0875 StartZ=0 EndX=117.223 EndY=-16.0875 EndZ=0
    g33: LineSegment StartX=117.223 StartY=-16.0875 StartZ=0 EndX=17.2232 EndY=-16.0875 EndZ=0
    g34: LineSegment StartX=17.2232 StartY=-16.0875 StartZ=0 EndX=17.2232 EndY=-19.0875 EndZ=0
    g35: LineSegment StartX=28.8094 StartY=-19.0875 StartZ=0 EndX=17.2232 EndY=-19.0875 EndZ=0
    g36: LineSegment StartX=47.0443 StartY=-50.4712 StartZ=0 EndX=12.8789 EndY=-141.321 EndZ=0
    g37: LineSegment StartX=-195.441 StartY=-127.082 StartZ=0 EndX=-196.497 EndY=-129.89 EndZ=0
    g38: LineSegment StartX=85.2866 StartY=-36.8766 StartZ=0 EndX=78.9396 EndY=-53.7463 EndZ=0
    g39: LineSegment StartX=60.9579 StartY=-27.7053 StartZ=0 EndX=54.6191 EndY=-44.5532 EndZ=0
    g40: LineSegment StartX=68.0907 StartY=-82.7664 StartZ=0 EndX=61.7465 EndY=-99.6365 EndZ=0
    g41: LineSegment StartX=43.7619 StartY=-73.595 StartZ=0 EndX=37.426 EndY=-90.4435 EndZ=0
    g42: LineSegment StartX=50.885 StartY=-128.652 StartZ=0 EndX=44.5456 EndY=-145.522 EndZ=0
    g43: LineSegment StartX=26.5562 StartY=-119.481 StartZ=0 EndX=20.2251 EndY=-136.329 EndZ=0
    g44: LineSegment StartX=9.3071 StartY=-165.349 StartZ=0 EndX=2.97115 EndY=-182.197 EndZ=0
    g45: LineSegment StartX=33.6358 StartY=-174.52 StartZ=0 EndX=27.2917 EndY=-191.39 EndZ=0
  constraints (71):
    c: Block(g0)
    c: Block(g1)
    c: Block(g2)
    c: Block(g4)
    c: Block(g3)
    c: Block(g6)
    c: Block(g5)
    c: Block(g8)
    c: Block(g7)
    c: Weight(g9) = 1
    c: Equal(g9,g10)
    c: Equal(g9,g11)
    c: Equal(g9,g12)
    c: InternalAlignment(g9-g12 -> g13) x4
    c: InternalAlignment(g14,g13)
    c: InternalAlignment(g15,g13)
    c: Block(g16)
    c: Weight(g17) = 1
    c: Equal(g17,g18)
    c: Equal(g17,g19)
    c: InternalAlignment(g17,g20)
    c: InternalAlignment(g18,g20)
    c: InternalAlignment(g19,g20)
    c: InternalAlignment(g21,g20)
    c: InternalAlignment(g22,g20)
    c: Block(g20)
    c: Block(g23)
    c: Block(g24)
    c: Block(g25)
    c: Block(g26)
    c: Block(g27)
    c: Block(g28)
    c: Coincident(g29,g28)
    c: Coincident(g29,g0)
    c: Block(g13)
    c: Coincident(g31,g30)
    c: Coincident(g31,g28)
    c: Block(g31)
    c: Coincident(g32,g0)
    c: Vertical(g32)
    c: Coincident(g33,g32)
    c: Horizontal(g33)
    c: Coincident(g34,g33)
    c: Vertical(g34)
    c: Block(g33)
    c: Coincident(g35,g13)
    c: Coincident(g35,g34)
    c: Horizontal(g35)
    c: Coincident(g36,g13)
    c: Coincident(g36,g20)
    c: Coincident(g37,g20)
    c: Coincident(g37,g30)
    c: Block(g30)
    c: Coincident(g38,g1)
    c: Coincident(g38,g2)
    c: Coincident(g39,g1)
    c: Coincident(g39,g2)
    c: Coincident(g40,g3)
    c: Coincident(g40,g4)
    c: Coincident(g41,g3)
    c: Coincident(g41,g4)
    c: Coincident(g42,g5)
    c: Coincident(g42,g6)
    c: Coincident(g43,g5)
    c: Coincident(g43,g6)
    c: Coincident(g44,g7)
    c: Coincident(g44,g8)
    c: Coincident(g45,g7)
    c: Coincident(g45,g8)
    c: Distance(g30) = 256
    c: Distance(g33) = 100
FEATURE [Part::Extrusion] Extrude002
  Base = -> Sketch001
  Dir = (1,0,0)
  DirMode = 2
  FaceMakerClass = Part::FaceMakerBullseye
  LengthFwd = 8
  LengthRev = 0
  Solid = true
  Symmetric = false
FEATURE [Sketcher::SketchObject] Sketch002
  FullyConstrained = true
  sketch-geometry (20):
    g0: LineSegment StartX=-2.77179 StartY=-200.304 StartZ=0 EndX=5.22821 EndY=-200.304 EndZ=0
    g1: LineSegment StartX=5.22821 StartY=-200.304 StartZ=0 EndX=5.22821 EndY=-197.304 EndZ=0
    g2: LineSegment StartX=-2.77179 StartY=-200.304 StartZ=0 EndX=-2.77179 EndY=-197.304 EndZ=0
    g3: LineSegment StartX=5.22821 StartY=-197.304 StartZ=0 EndX=8.22821 EndY=-197.304 EndZ=0
    g4: LineSegment StartX=-2.77179 StartY=-197.304 StartZ=0 EndX=-5.77179 EndY=-197.304 EndZ=0
    g5: LineSegment StartX=19.2282 StartY=-203.304 StartZ=0 EndX=19.2282 EndY=-206.304 EndZ=0
    g6: LineSegment StartX=-16.7718 StartY=-203.304 StartZ=0 EndX=-16.7718 EndY=-206.304 EndZ=0
    g7: LineSegment StartX=-16.7718 StartY=-206.304 StartZ=0 EndX=19.2282 EndY=-206.304 EndZ=0
    g8: Circle CenterX=-16.7718 CenterY=-203.304 CenterZ=0 NormalX=0 NormalY=0 NormalZ=1 AngleXU=0 Radius=1
    g9: Circle CenterX=-5.77179 CenterY=-203.304 CenterZ=0 NormalX=0 NormalY=0 NormalZ=1 AngleXU=0 Radius=1
    g10: Circle CenterX=-5.77179 CenterY=-197.304 CenterZ=0 NormalX=0 NormalY=0 NormalZ=1 AngleXU=0 Radius=1
    g11: BSplineCurve PolesCount=3 KnotsCount=2 Degree=2 IsPeriodic=0
    g12: GeomPoint X=-16.7718 Y=-203.304 Z=0
    g13: GeomPoint X=-5.77179 Y=-197.304 Z=0
    g14: Circle CenterX=19.2282 CenterY=-203.304 CenterZ=0 NormalX=0 NormalY=0 NormalZ=1 AngleXU=0 Radius=1
    g15: Circle CenterX=8.22821 CenterY=-203.304 CenterZ=0 NormalX=0 NormalY=0 NormalZ=1 AngleXU=0 Radius=1
    g16: Circle CenterX=8.22821 CenterY=-197.304 CenterZ=0 NormalX=0 NormalY=0 NormalZ=1 AngleXU=0 Radius=1
    g17: BSplineCurve PolesCount=3 KnotsCount=2 Degree=2 IsPeriodic=0
    g18: GeomPoint X=19.2282 Y=-203.304 Z=0
    g19: GeomPoint X=8.22821 Y=-197.304 Z=0
  constraints (41):
    c: Horizontal(g0)
    c: Distance(g0) = 8
    c: Coincident(g1,g0)
    c: Vertical(g1)
    c: Distance(g1) = 3
    c: Coincident(g2,g0)
    c: Vertical(g2)
    c: Distance(g2) = 3
    c: Coincident(g3,g1)
    c: Horizontal(g3)
    c: Distance(g3) = 3
    c: Coincident(g4,g2)
    c: Horizontal(g4)
    c: Distance(g4) = 3
    c: Vertical(g5)
    c: Vertical(g6)
    c: Coincident(g7,g6)
    c: Coincident(g7,g5)
    c: Weight(g8) = 1
    c: Equal(g8,g9)
    c: Equal(g8,g10)
    c: Coincident(g11,g4)
    c: InternalAlignment(g8,g11)
    c: InternalAlignment(g9,g11)
    c: InternalAlignment(g10,g11)
    c: InternalAlignment(g12,g11)
    c: InternalAlignment(g13,g11)
    c: Coincident(g17,g5)
    c: Weight(g14) = 1
    c: Equal(g14,g15)
    c: Equal(g14,g16)
    c: Coincident(g17,g3)
    c: InternalAlignment(g14,g17)
    c: InternalAlignment(g15,g17)
    c: InternalAlignment(g16,g17)
    c: InternalAlignment(g18,g17)
    c: InternalAlignment(g19,g17)
    c: Block(g7)
    c: Block(g17)
    c: Block(g11)
    c: Block(g6)
FEATURE [Part::Extrusion] Extrude003
  Base = -> Sketch002
  Dir = (0,0,1)
  DirMode = 2
  FaceMakerClass = Part::FaceMakerBullseye
  LengthFwd = 260
  LengthRev = 0
  Solid = true
  Symmetric = false
FEATURE [Part::Extrusion] Extrude
  Base = -> Sketch
  Dir = (0,0,1)
  DirMode = 2
  FaceMakerClass = Part::FaceMakerBullseye
  LengthFwd = 14
  LengthRev = 0
  Solid = true
  Symmetric = false
